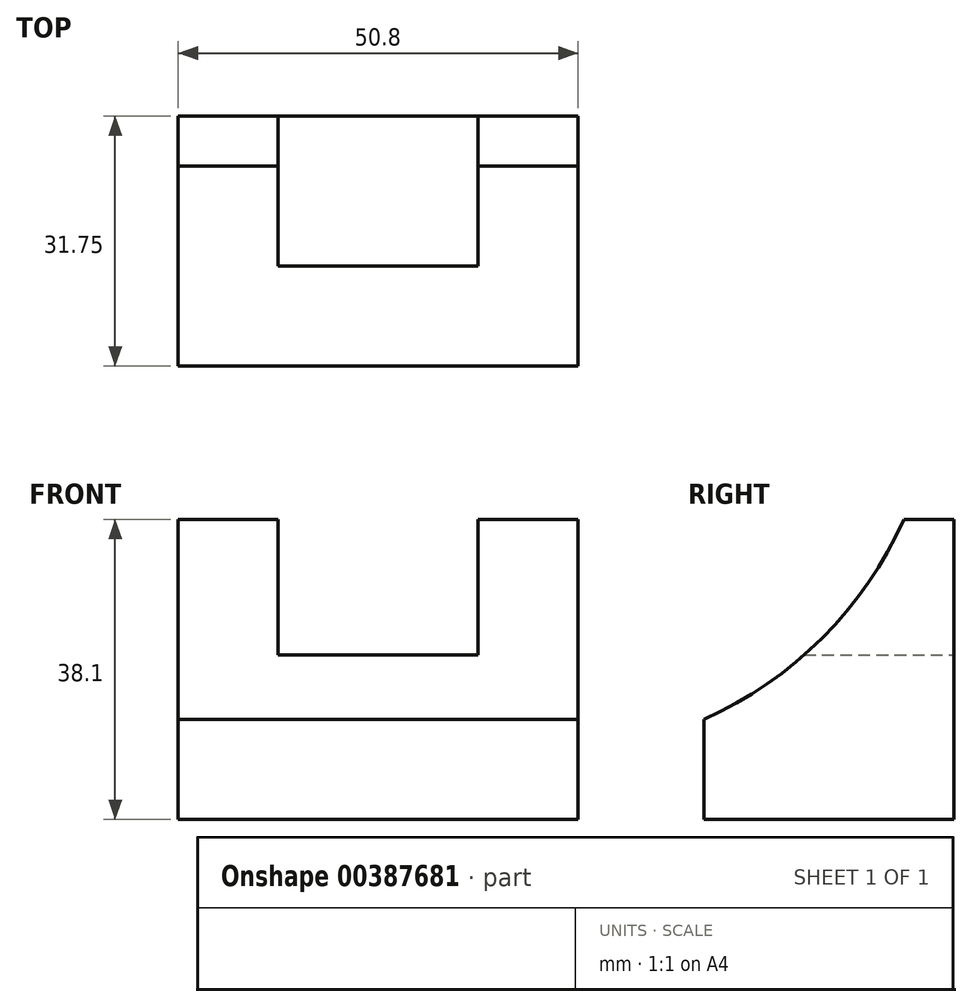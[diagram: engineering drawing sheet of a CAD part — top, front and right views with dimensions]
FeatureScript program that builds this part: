
annotation { "Feature Type Name" : "Feature", "Feature Type Description" : "" }
export const myFeature = defineFeature(function(context is Context, id is Id, definition is map)
    precondition{}
    {
        {
            var Q0;
            Q0=qCreatedBy(makeId("Front.planeOp"),FACE);
            var sketch = newSketch(context, id + "F0", { "sketchPlane" : qUnion([Q0])});
            skLineSegment(sketch, "E0", {"start": v(0, 0) * mm, "end": v(50.8, 0) * mm});
            skLineSegment(sketch, "E1", {"start": v(50.8, 0) * mm, "end": v(50.8, 38.1) * mm});
            skLineSegment(sketch, "E2", {"start": v(50.8, 38.1) * mm, "end": v(0, 38.1) * mm});
            skLineSegment(sketch, "E3", {"start": v(0, 38.1) * mm, "end": v(0, 0) * mm});
            skSolve(sketch);
        }
        {
            var Q0;
            Q0=makeQuery(id+"F0.imprint","IMPRINT",FACE,{"disambiguationData":[TD([[makeQuery(id+"F0.imprint","IMPRINT",EDGE,{"derivedFrom":sQuery(id+"F0.wireOp",EDGE,"E0")}),1.0]])]});
            extrude(context, id + "F1", {"entities" : qUnion([Q0]), "depth" : 31.75 * mm});
        }
        {
            var Q0;
            Q0=makeQuery(id+"F1.opExtrude","SWEPT_FACE",FACE,{"disambiguationData":[OSD([sQuery(id+"F0.wireOp",EDGE,"E1")])]});
            var sketch = newSketch(context, id + "F2", { "sketchPlane" : qUnion([Q0])});
            skArc(sketch, "E4", {"start": v(-31.75, 12.7) * mm, "mid": v(-16.73, 23.08) * mm, "end": v(-6.35, 38.1) * mm});
            skSolve(sketch);
        }
        {
            var Q0;
            {var subQ0=sQuery(id+"F2.wireOp",EDGE,"E4");Q0=makeQuery(id+"F2.imprint","IMPRINT",FACE,{"disambiguationData":[TD([[makeQuery(id+"F2.imprint","IMPRINT",EDGE,{"derivedFrom":subQ0}),1.0]])]});}
            extrude(context, id + "F3", {"entities" : qUnion([Q0]), "operationType" : NewBodyOperationType.REMOVE, "oppositeDirection" : true, "depth" : 50.8 * mm});
        }
        {
            var Q0;
            Q0=makeQuery(id+"F1.opExtrude","CAP_FACE",FACE,{"disambiguationData":[OSD([sQuery(id+"F0.wireOp",EDGE,"E0"),sQuery(id+"F0.wireOp",EDGE,"E1"),sQuery(id+"F0.wireOp",EDGE,"E2"),sQuery(id+"F0.wireOp",EDGE,"E3")])],"isStart":true});
            var sketch = newSketch(context, id + "F4", { "sketchPlane" : qUnion([Q0])});
            skLineSegment(sketch, "E5", {"start": v(-38.1, 38.1) * mm, "end": v(-38.1, 20.87) * mm});
            skLineSegment(sketch, "E6", {"start": v(-38.1, 20.87) * mm, "end": v(-12.7, 20.87) * mm});
            skLineSegment(sketch, "E7", {"start": v(-12.7, 20.87) * mm, "end": v(-12.7, 38.1) * mm});
            skSolve(sketch);
        }
        {
            var Q0;
            {var subQ0=sQuery(id+"F4.wireOp",EDGE,"E5");Q0=makeQuery(id+"F4.imprint","IMPRINT",FACE,{"disambiguationData":[TD([[makeQuery(id+"F4.imprint","IMPRINT",EDGE,{"derivedFrom":subQ0}),1.0]])]});}
            extrude(context, id + "F5", {"entities" : qUnion([Q0]), "operationType" : NewBodyOperationType.REMOVE, "oppositeDirection" : true, "depth" : 19.05 * mm});
        }
    });
